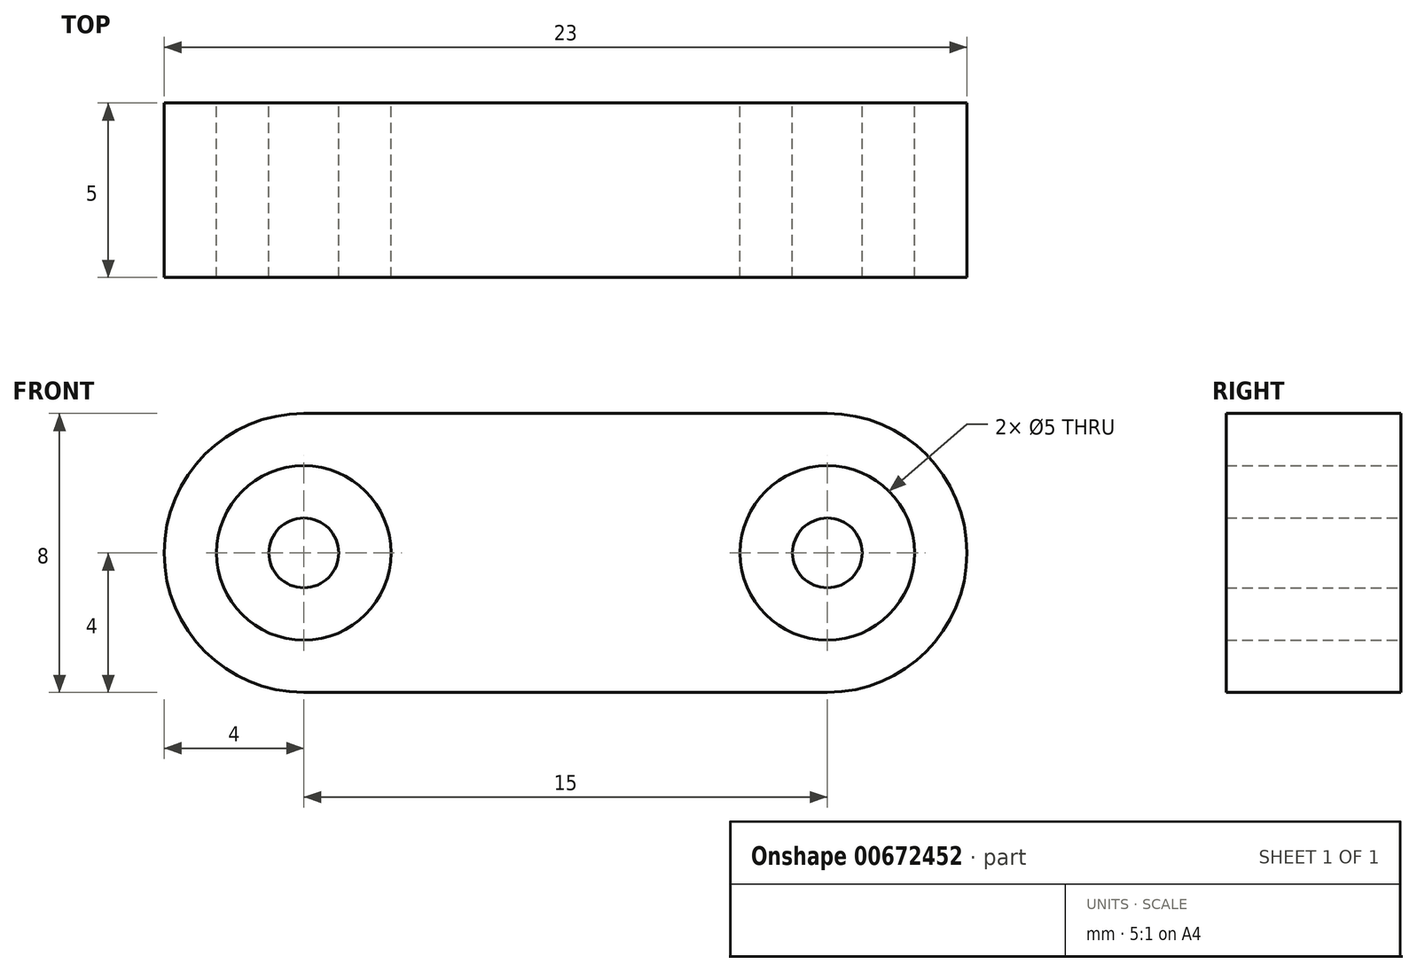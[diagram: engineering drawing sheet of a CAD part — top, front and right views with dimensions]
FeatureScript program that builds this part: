
annotation { "Feature Type Name" : "Feature", "Feature Type Description" : "" }
export const myFeature = defineFeature(function(context is Context, id is Id, definition is map)
    precondition{}
    {
        {
            var Q0;
            Q0=qCreatedBy(makeId("Front.planeOp"),FACE);
            var sketch = newSketch(context, id + "F0", { "sketchPlane" : qUnion([Q0])});
            skArc(sketch, "E0", {"start": v(0, 4) * mm, "mid": v(-4, 0) * mm, "end": v(0, -4) * mm});
            skCircle(sketch, "E1", {"center": v(0, 0) * mm, "radius": 2.5 * mm});
            skArc(sketch, "E2", {"start": v(15, -4) * mm, "mid": v(19, 0) * mm, "end": v(15, 4) * mm});
            skCircle(sketch, "E3", {"center": v(15, 0) * mm, "radius": 2.5 * mm});
            skLineSegment(sketch, "E4", {"start": v(0, 4) * mm, "end": v(15, 4) * mm});
            skLineSegment(sketch, "E5", {"start": v(0, -4) * mm, "end": v(15, -4) * mm});
            skCircle(sketch, "E6", {"center": v(0, 0) * mm, "radius": 1 * mm});
            skCircle(sketch, "E7", {"center": v(15, 0) * mm, "radius": 1 * mm});
            skSolve(sketch);
        }
        {
            var Q0;
            Q0=makeQuery(id+"F0.imprint","IMPRINT",FACE,{"disambiguationData":[TD([[makeQuery(id+"F0.imprint","IMPRINT",EDGE,{"derivedFrom":sQuery(id+"F0.wireOp",EDGE,"E0")}),1.0]])]});
            var Q1;
            Q1=makeQuery(id+"F0.imprint","IMPRINT",FACE,{"disambiguationData":[TD([[makeQuery(id+"F0.imprint","IMPRINT",EDGE,{"derivedFrom":sQuery(id+"F0.wireOp",EDGE,"E6")}),1.0]])]});
            var Q2;
            Q2=makeQuery(id+"F0.imprint","IMPRINT",FACE,{"disambiguationData":[TD([[makeQuery(id+"F0.imprint","IMPRINT",EDGE,{"derivedFrom":sQuery(id+"F0.wireOp",EDGE,"E7")}),1.0]])]});
            extrude(context, id + "F1", {"entities" : qUnion([Q0, Q1, Q2]), "endBound" : BoundingType.SYMMETRIC, "depth" : 5 * mm, "offsetDistance" : 25 * mm});
        }
    });
